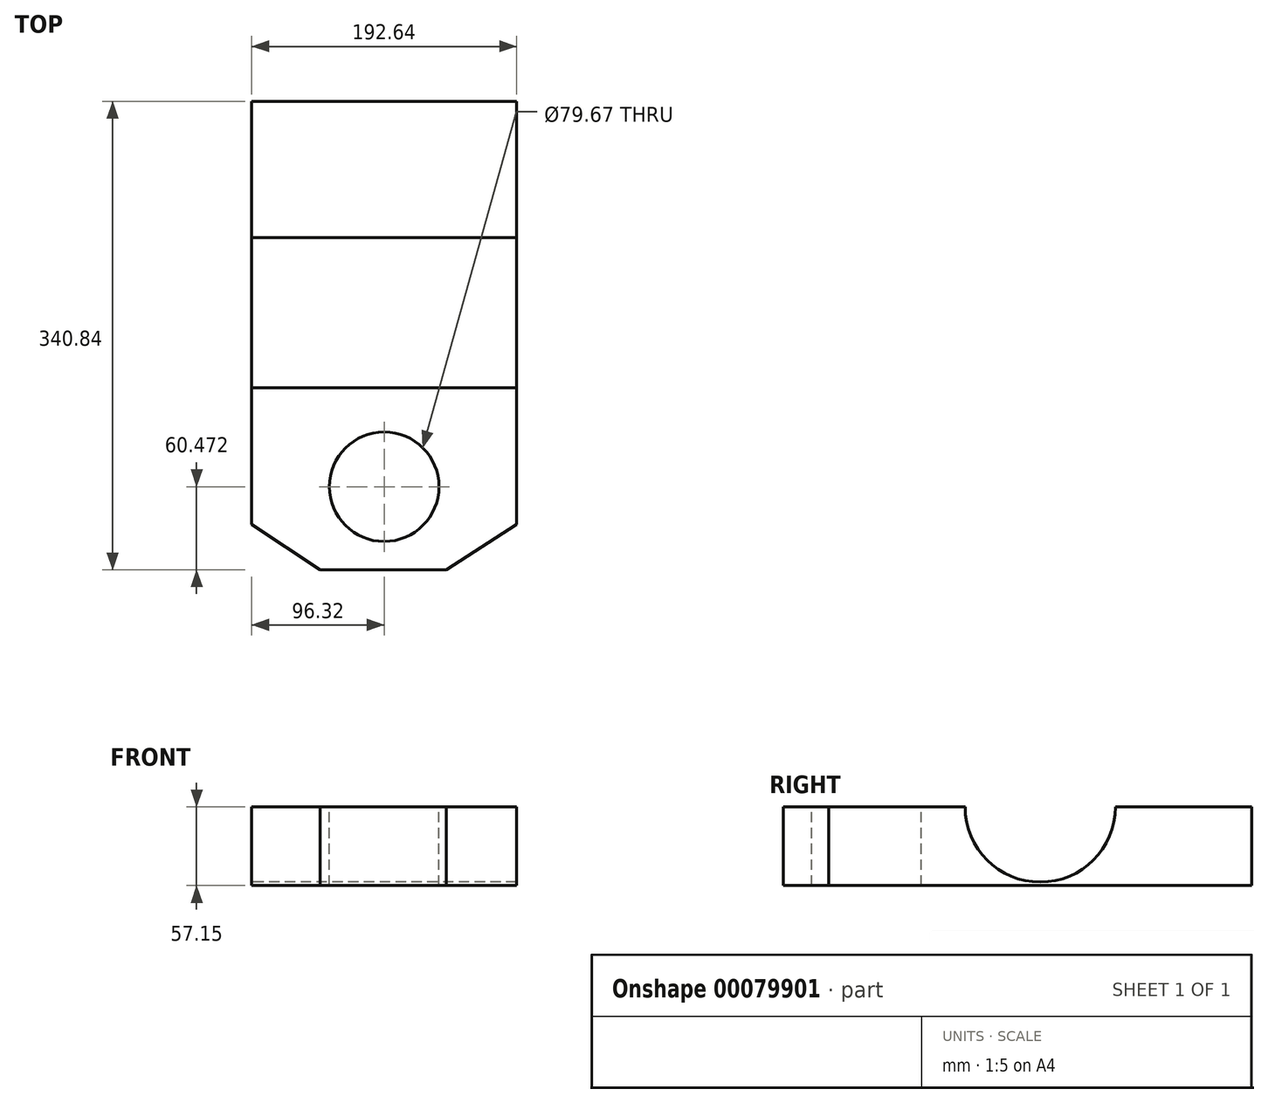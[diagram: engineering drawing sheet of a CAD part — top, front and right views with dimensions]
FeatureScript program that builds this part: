
annotation { "Feature Type Name" : "Feature", "Feature Type Description" : "" }
export const myFeature = defineFeature(function(context is Context, id is Id, definition is map)
    precondition{}
    {
        {
            var Q0;
            Q0=qCreatedBy(makeId("Top.planeOp"),FACE);
            var sketch = newSketch(context, id + "F0", { "sketchPlane" : qUnion([Q0])});
            skLineSegment(sketch, "E0.bottom", {"start": v(96.32, 108.2) * mm, "end": v(-96.32, 108.2) * mm});
            skLineSegment(sketch, "E0.top", {"start": v(96.32, -108.2) * mm, "end": v(-96.32, -108.2) * mm});
            skLineSegment(sketch, "E0.left", {"start": v(96.32, 108.2) * mm, "end": v(96.32, -108.2) * mm});
            skLineSegment(sketch, "E0.right", {"start": v(-96.32, 108.2) * mm, "end": v(-96.32, -108.2) * mm});
            skPoint(sketch, "E0.middle", {"position": v(0, 0) * mm});
            skSolve(sketch);
        }
        {
            var Q0;
            Q0=makeQuery(id+"F0.imprint","IMPRINT",FACE,{"disambiguationData":[TD([[makeQuery(id+"F0.imprint","IMPRINT",EDGE,{"derivedFrom":sQuery(id+"F0.wireOp",EDGE,"E0.bottom")}),1.0]])]});
            extrude(context, id + "F1", {"entities" : qUnion([Q0]), "oppositeDirection" : true, "depth" : 57.15 * mm});
        }
        {
            var Q0;
            Q0=makeQuery(id+"F1.opExtrude","CAP_FACE",FACE,{"disambiguationData":[OSD([sQuery(id+"F0.wireOp",EDGE,"E0.bottom"),sQuery(id+"F0.wireOp",EDGE,"E0.top"),sQuery(id+"F0.wireOp",EDGE,"E0.left"),sQuery(id+"F0.wireOp",EDGE,"E0.right")])],"isStart":true});
            var sketch = newSketch(context, id + "F2", { "sketchPlane" : qUnion([Q0])});
            skLineSegment(sketch, "E1.bottom", {"start": v(-96.32, -108.2) * mm, "end": v(96.32, -108.2) * mm});
            skLineSegment(sketch, "E1.top", {"start": v(-46.5, -232.65) * mm, "end": v(45.2, -232.65) * mm});
            skLineSegment(sketch, "E1.left", {"start": v(-96.32, -108.2) * mm, "end": v(-96.32, -199.63) * mm});
            skLineSegment(sketch, "E1.right", {"start": v(96.32, -108.2) * mm, "end": v(96.32, -199.63) * mm});
            skCircle(sketch, "E2", {"center": v(0, -172.18) * mm, "radius": 39.83 * mm});
            skLineSegment(sketch, "E3", {"start": v(-96.32, -199.63) * mm, "end": v(-46.5, -232.65) * mm});
            skLineSegment(sketch, "E4", {"start": v(96.32, -199.63) * mm, "end": v(45.2, -232.65) * mm});
            skSolve(sketch);
        }
        {
            var Q0;
            Q0=makeQuery(id+"F2.imprint","IMPRINT",FACE,{"disambiguationData":[TD([[makeQuery(id+"F2.imprint","IMPRINT",EDGE,{"derivedFrom":sQuery(id+"F2.wireOp",EDGE,"E1.bottom")}),1.0]])]});
            extrude(context, id + "F3", {"entities" : qUnion([Q0]), "operationType" : NewBodyOperationType.ADD, "oppositeDirection" : true, "depth" : 57.15 * mm});
        }
        {
            var Q0;
            Q0=makeQuery(id+"F1.opExtrude","SWEPT_FACE",FACE,{"disambiguationData":[OSD([sQuery(id+"F0.wireOp",EDGE,"E0.right")])]});
            var sketch = newSketch(context, id + "F4", { "sketchPlane" : qUnion([Q0])});
            skPoint(sketch, "E5", {"position": v(45.72, 0) * mm});
            skSolve(sketch);
        }
        {
            var Q0;
            Q0=sQuery(id+"F4.wireOp",VERTEX,"E5");
            var Q1;
            Q1=makeQuery(id+"F1.opExtrude","SWEPT_BODY",BODY,{"disambiguationData":[OSD([sQuery(id+"F0.wireOp",EDGE,"E0.bottom"),sQuery(id+"F0.wireOp",EDGE,"E0.top"),sQuery(id+"F0.wireOp",EDGE,"E0.left"),sQuery(id+"F0.wireOp",EDGE,"E0.right")])]});
            hole(context, id + "F5", {"style" : HoleStyle.SIMPLE, "endStyle" : HoleEndStyle.THROUGH, "holeDiameter" : 109.22 * mm, "locations" : qUnion([Q0]), "scope" : qUnion([Q1]), "isTappedThrough" : true});
        }
    });
